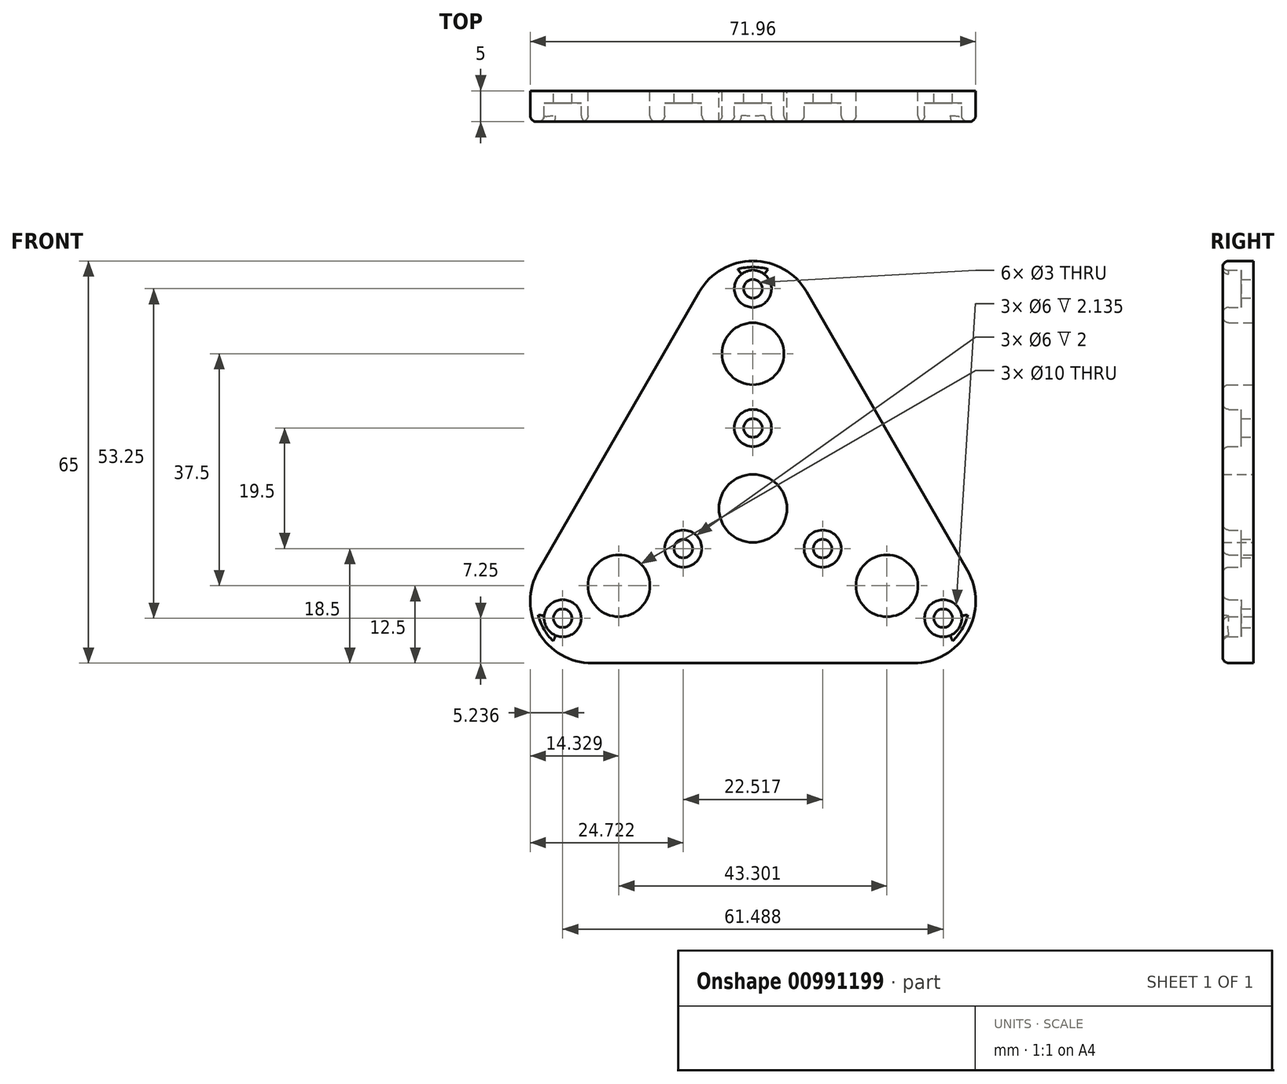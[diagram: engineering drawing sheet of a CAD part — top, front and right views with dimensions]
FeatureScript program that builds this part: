
annotation { "Feature Type Name" : "Feature", "Feature Type Description" : "" }
export const myFeature = defineFeature(function(context is Context, id is Id, definition is map)
    precondition{}
    {
        {
            var Q0;
            Q0=qCreatedBy(makeId("Front.planeOp"),FACE);
            var sketch = newSketch(context, id + "F0", { "sketchPlane" : qUnion([Q0])});
            skCircle(sketch, "E0", {"center": v(0, 0) * mm, "radius": 25 * mm, "construction": true});
            skLineSegment(sketch, "E1.0", {"start": v(25.98, -25) * mm, "end": v(-25.98, -25) * mm});
            skLineSegment(sketch, "E1.1", {"start": v(-34.64, -10) * mm, "end": v(-8.66, 35) * mm});
            skLineSegment(sketch, "E1.2", {"start": v(8.66, 35) * mm, "end": v(34.64, -10) * mm});
            skPoint(sketch, "E1.0.midPoint", {"position": v(0, -25) * mm});
            skPoint(sketch, "E2.visualSharp", {"position": v(-43.3, -25) * mm});
            skArc(sketch, "E2.filletArc", {"start": v(-34.64, -10) * mm, "mid": v(-34.64, -20) * mm, "end": v(-25.98, -25) * mm});
            skPoint(sketch, "E3.visualSharp", {"position": v(43.3, -25) * mm});
            skArc(sketch, "E3.filletArc", {"start": v(25.98, -25) * mm, "mid": v(34.64, -20) * mm, "end": v(34.64, -10) * mm});
            skPoint(sketch, "E4.visualSharp", {"position": v(0, 50) * mm});
            skArc(sketch, "E4.filletArc", {"start": v(8.66, 35) * mm, "mid": v(0, 40) * mm, "end": v(-8.66, 35) * mm});
            skLineSegment(sketch, "E5", {"start": v(-34.64, -20) * mm, "end": v(0, 0) * mm, "construction": true});
            skLineSegment(sketch, "E6", {"start": v(0, 0) * mm, "end": v(0, 40) * mm, "construction": true});
            skCircle(sketch, "E7", {"center": v(0, 25) * mm, "radius": 5 * mm});
            skCircle(sketch, "E8", {"center": v(21.65, -12.5) * mm, "radius": 5 * mm});
            skCircle(sketch, "E9", {"center": v(-21.65, -12.5) * mm, "radius": 5 * mm});
            skCircle(sketch, "E10", {"center": v(0, 0) * mm, "radius": 5.5 * mm});
            skCircle(sketch, "E11", {"center": v(0, 13) * mm, "radius": 3 * mm});
            skCircle(sketch, "E12", {"center": v(11.26, -6.5) * mm, "radius": 3 * mm});
            skCircle(sketch, "E13", {"center": v(-11.26, -6.5) * mm, "radius": 3 * mm});
            skCircle(sketch, "E14", {"center": v(30.74, -17.75) * mm, "radius": 3 * mm});
            skCircle(sketch, "E15", {"center": v(0, 35.5) * mm, "radius": 3 * mm});
            skCircle(sketch, "E16", {"center": v(-30.74, -17.75) * mm, "radius": 3 * mm});
            skLineSegment(sketch, "E17", {"start": v(0, 0) * mm, "end": v(34.64, -20) * mm, "construction": true});
            skCircle(sketch, "E18", {"center": v(-30.74, -17.75) * mm, "radius": 1.5 * mm});
            skCircle(sketch, "E19", {"center": v(-11.26, -6.5) * mm, "radius": 1.5 * mm});
            skCircle(sketch, "E20", {"center": v(11.26, -6.5) * mm, "radius": 1.5 * mm});
            skCircle(sketch, "E21", {"center": v(30.74, -17.75) * mm, "radius": 1.5 * mm});
            skCircle(sketch, "E22", {"center": v(0, 13) * mm, "radius": 1.5 * mm});
            skCircle(sketch, "E23", {"center": v(0, 35.5) * mm, "radius": 1.5 * mm});
            skSolve(sketch);
        }
        {
            var Q0;
            Q0 = qSketchRegion(id + "F0", true);
            extrude(context, id + "F1", {"entities" : qUnion([Q0]), "depth" : 5 * mm, "offsetDistance" : 25 * mm});
        }
        {
            var Q0;
            Q0=makeQuery(id+"F0.imprint","IMPRINT",FACE,{"disambiguationData":[TD([[makeQuery(id+"F0.imprint","IMPRINT",EDGE,{"derivedFrom":sQuery(id+"F0.wireOp",EDGE,"E16")}),1.0]])]});
            var Q1;
            Q1=makeQuery(id+"F0.imprint","IMPRINT",FACE,{"disambiguationData":[TD([[makeQuery(id+"F0.imprint","IMPRINT",EDGE,{"derivedFrom":sQuery(id+"F0.wireOp",EDGE,"E13")}),1.0]])]});
            var Q2;
            Q2=makeQuery(id+"F0.imprint","IMPRINT",FACE,{"disambiguationData":[TD([[makeQuery(id+"F0.imprint","IMPRINT",EDGE,{"derivedFrom":sQuery(id+"F0.wireOp",EDGE,"E12")}),1.0]])]});
            var Q3;
            Q3=makeQuery(id+"F0.imprint","IMPRINT",FACE,{"disambiguationData":[TD([[makeQuery(id+"F0.imprint","IMPRINT",EDGE,{"derivedFrom":sQuery(id+"F0.wireOp",EDGE,"E14")}),1.0]])]});
            var Q4;
            Q4=makeQuery(id+"F0.imprint","IMPRINT",FACE,{"disambiguationData":[TD([[makeQuery(id+"F0.imprint","IMPRINT",EDGE,{"derivedFrom":sQuery(id+"F0.wireOp",EDGE,"E11")}),1.0]])]});
            var Q5;
            Q5=makeQuery(id+"F0.imprint","IMPRINT",FACE,{"disambiguationData":[TD([[makeQuery(id+"F0.imprint","IMPRINT",EDGE,{"derivedFrom":sQuery(id+"F0.wireOp",EDGE,"E15")}),1.0]])]});
            extrude(context, id + "F2", {"entities" : qUnion([Q0, Q1, Q2, Q3, Q4, Q5]), "operationType" : NewBodyOperationType.ADD, "depth" : 2 * mm, "offsetDistance" : 25 * mm});
        }
        {
            var Q0;
            Q0=makeQuery(id+"F1.opExtrude","CAP_EDGE",EDGE,{"disambiguationData":[OSD([sQuery(id+"F0.wireOp",EDGE,"E1.1")])],"isStart":false});
            var Q1;
            Q1=makeQuery(id+"F1.opExtrude","CAP_EDGE",EDGE,{"disambiguationData":[OSD([sQuery(id+"F0.wireOp",EDGE,"E4.filletArc")])],"isStart":false});
            var Q2;
            Q2=makeQuery(id+"F1.opExtrude","CAP_EDGE",EDGE,{"disambiguationData":[OSD([sQuery(id+"F0.wireOp",EDGE,"E1.2")])],"isStart":false});
            var Q3;
            Q3=makeQuery(id+"F1.opExtrude","CAP_EDGE",EDGE,{"disambiguationData":[OSD([sQuery(id+"F0.wireOp",EDGE,"E3.filletArc")])],"isStart":false});
            var Q4;
            Q4=makeQuery(id+"F1.opExtrude","CAP_EDGE",EDGE,{"disambiguationData":[OSD([sQuery(id+"F0.wireOp",EDGE,"E1.0")])],"isStart":false});
            var Q5;
            Q5=makeQuery(id+"F1.opExtrude","CAP_EDGE",EDGE,{"disambiguationData":[OSD([sQuery(id+"F0.wireOp",EDGE,"E2.filletArc")])],"isStart":false});
            fillet(context, id + "F3", {"entities" : qUnion([Q0, Q1, Q2, Q3, Q4, Q5]), "radius" : 1 * mm, "tangentPropagation" : true, "allowEdgeOverflow" : false});
        }
        {
            var Q0;
            Q0=makeQuery(id+"F1.opExtrude","CAP_EDGE",EDGE,{"disambiguationData":[OSD([sQuery(id+"F0.wireOp",EDGE,"E11")])],"isStart":false});
            var Q1;
            Q1=makeQuery(id+"F1.opExtrude","CAP_EDGE",EDGE,{"disambiguationData":[OSD([sQuery(id+"F0.wireOp",EDGE,"E12")])],"isStart":false});
            var Q2;
            Q2=makeQuery(id+"F1.opExtrude","CAP_EDGE",EDGE,{"disambiguationData":[OSD([sQuery(id+"F0.wireOp",EDGE,"E13")])],"isStart":false});
            var Q3;
            Q3=makeQuery(id+"F1.opExtrude","CAP_EDGE",EDGE,{"disambiguationData":[OSD([sQuery(id+"F0.wireOp",EDGE,"E7")])],"isStart":false});
            var Q4;
            Q4=makeQuery(id+"F1.opExtrude","CAP_EDGE",EDGE,{"disambiguationData":[OSD([sQuery(id+"F0.wireOp",EDGE,"E8")])],"isStart":false});
            var Q5;
            Q5=makeQuery(id+"F1.opExtrude","CAP_EDGE",EDGE,{"disambiguationData":[OSD([sQuery(id+"F0.wireOp",EDGE,"E9")])],"isStart":false});
            var Q6;
            Q6=makeQuery(id+"F1.opExtrude","CAP_EDGE",EDGE,{"disambiguationData":[OSD([sQuery(id+"F0.wireOp",EDGE,"E14")])],"isStart":false});
            var Q7;
            Q7=makeQuery(id+"F1.opExtrude","CAP_EDGE",EDGE,{"disambiguationData":[OSD([sQuery(id+"F0.wireOp",EDGE,"E16")])],"isStart":false});
            var Q8;
            Q8=makeQuery(id+"F1.opExtrude","CAP_EDGE",EDGE,{"disambiguationData":[OSD([sQuery(id+"F0.wireOp",EDGE,"E15")])],"isStart":false});
            fillet(context, id + "F4", {"entities" : qUnion([Q0, Q1, Q2, Q3, Q4, Q5, Q6, Q7, Q8]), "radius" : 1 * mm, "tangentPropagation" : true, "allowEdgeOverflow" : false});
        }
    });
